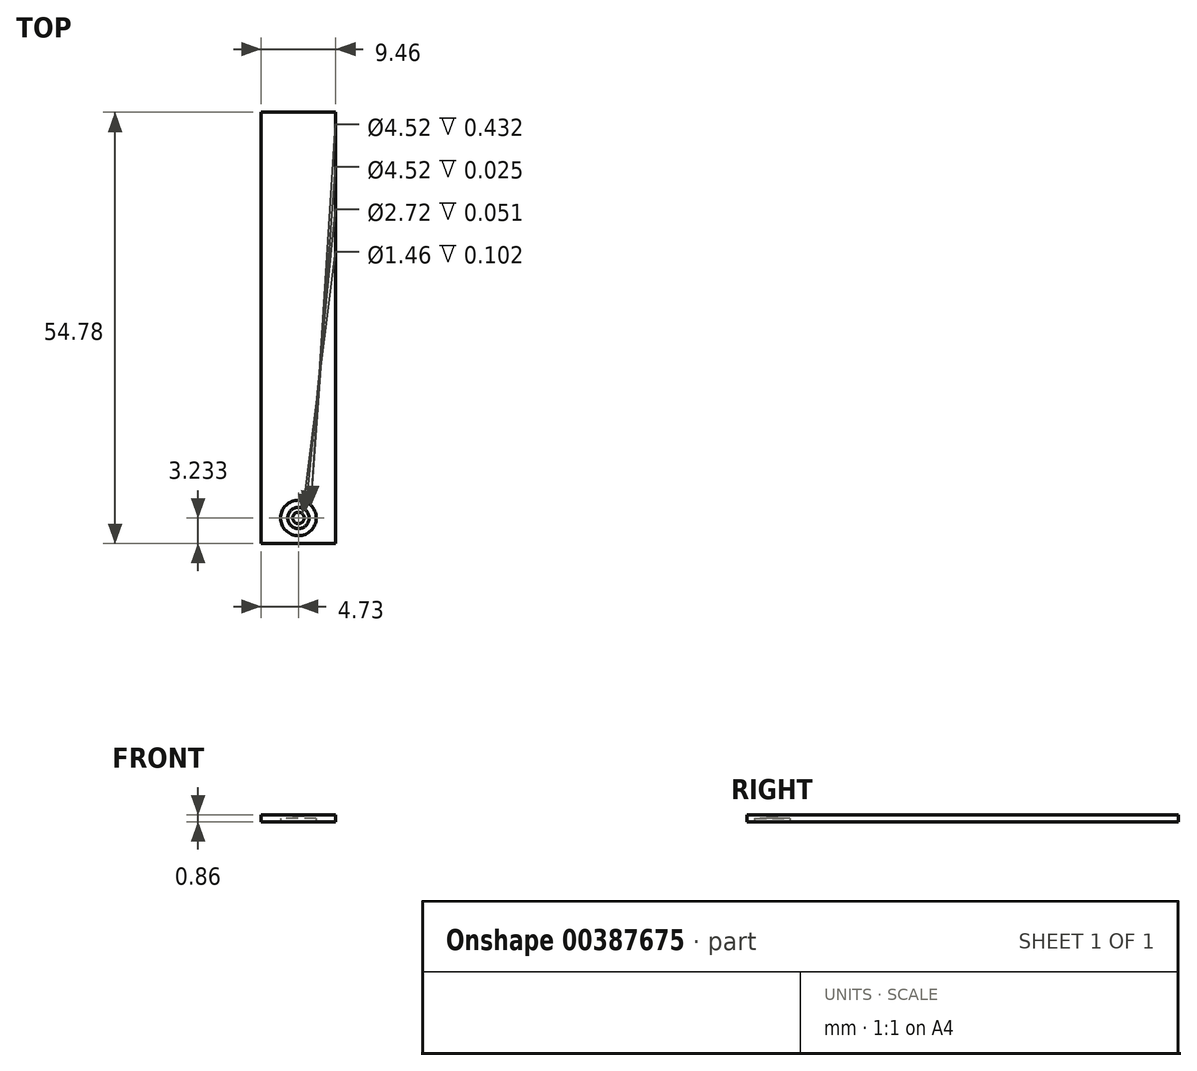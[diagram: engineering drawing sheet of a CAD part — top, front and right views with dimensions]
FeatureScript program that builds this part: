
annotation { "Feature Type Name" : "Feature", "Feature Type Description" : "" }
export const myFeature = defineFeature(function(context is Context, id is Id, definition is map)
    precondition{}
    {
        {
            var Q0;
            Q0=qCreatedBy(makeId("Top.planeOp"),FACE);
            var sketch = newSketch(context, id + "F0", { "sketchPlane" : qUnion([Q0])});
            skLineSegment(sketch, "E0.bottom", {"start": v(4.73, -27.4) * mm, "end": v(-4.73, -27.4) * mm});
            skLineSegment(sketch, "E0.top", {"start": v(4.73, 27.4) * mm, "end": v(-4.73, 27.4) * mm});
            skLineSegment(sketch, "E0.left", {"start": v(4.73, -27.4) * mm, "end": v(4.73, 27.4) * mm});
            skLineSegment(sketch, "E0.right", {"start": v(-4.73, -27.4) * mm, "end": v(-4.73, 27.4) * mm});
            skPoint(sketch, "E0.middle", {"position": v(0, 0) * mm});
            skCircle(sketch, "E1", {"center": v(0, -24.16) * mm, "radius": 0.73 * mm});
            skCircle(sketch, "E2", {"center": v(0, -24.16) * mm, "radius": 1.36 * mm});
            skCircle(sketch, "E3", {"center": v(0, -24.16) * mm, "radius": 2.26 * mm});
            skSolve(sketch);
        }
        {
            var Q0;
            Q0=makeQuery(id+"F0.imprint","IMPRINT",FACE,{"disambiguationData":[TD([[makeQuery(id+"F0.imprint","IMPRINT",EDGE,{"derivedFrom":sQuery(id+"F0.wireOp",EDGE,"E0.bottom")}),-1.0]])]});
            extrude(context, id + "F1", {"entities" : qUnion([Q0]), "endBound" : BoundingType.SYMMETRIC, "depth" : 0.86 * mm});
        }
        {
            var Q0;
            Q0=makeQuery(id+"F0.imprint","IMPRINT",FACE,{"disambiguationData":[TD([[makeQuery(id+"F0.imprint","IMPRINT",EDGE,{"derivedFrom":sQuery(id+"F0.wireOp",EDGE,"E2")}),-1.0]])]});
            extrude(context, id + "F2", {"entities" : qUnion([Q0]), "operationType" : NewBodyOperationType.ADD, "depth" : 0.4 * mm});
        }
        {
            var Q0;
            Q0=makeQuery(id+"F0.imprint","IMPRINT",FACE,{"disambiguationData":[TD([[makeQuery(id+"F0.imprint","IMPRINT",EDGE,{"derivedFrom":sQuery(id+"F0.wireOp",EDGE,"E1")}),-1.0]])]});
            extrude(context, id + "F3", {"entities" : qUnion([Q0]), "operationType" : NewBodyOperationType.ADD, "depth" : 0.36 * mm});
        }
        {
            var Q0;
            Q0=makeQuery(id+"F0.imprint","IMPRINT",FACE,{"disambiguationData":[TD([[makeQuery(id+"F0.imprint","IMPRINT",EDGE,{"derivedFrom":sQuery(id+"F0.wireOp",EDGE,"E1")}),1.0]])]});
            extrude(context, id + "F4", {"entities" : qUnion([Q0]), "operationType" : NewBodyOperationType.ADD, "depth" : 0.25 * mm});
        }
    });
